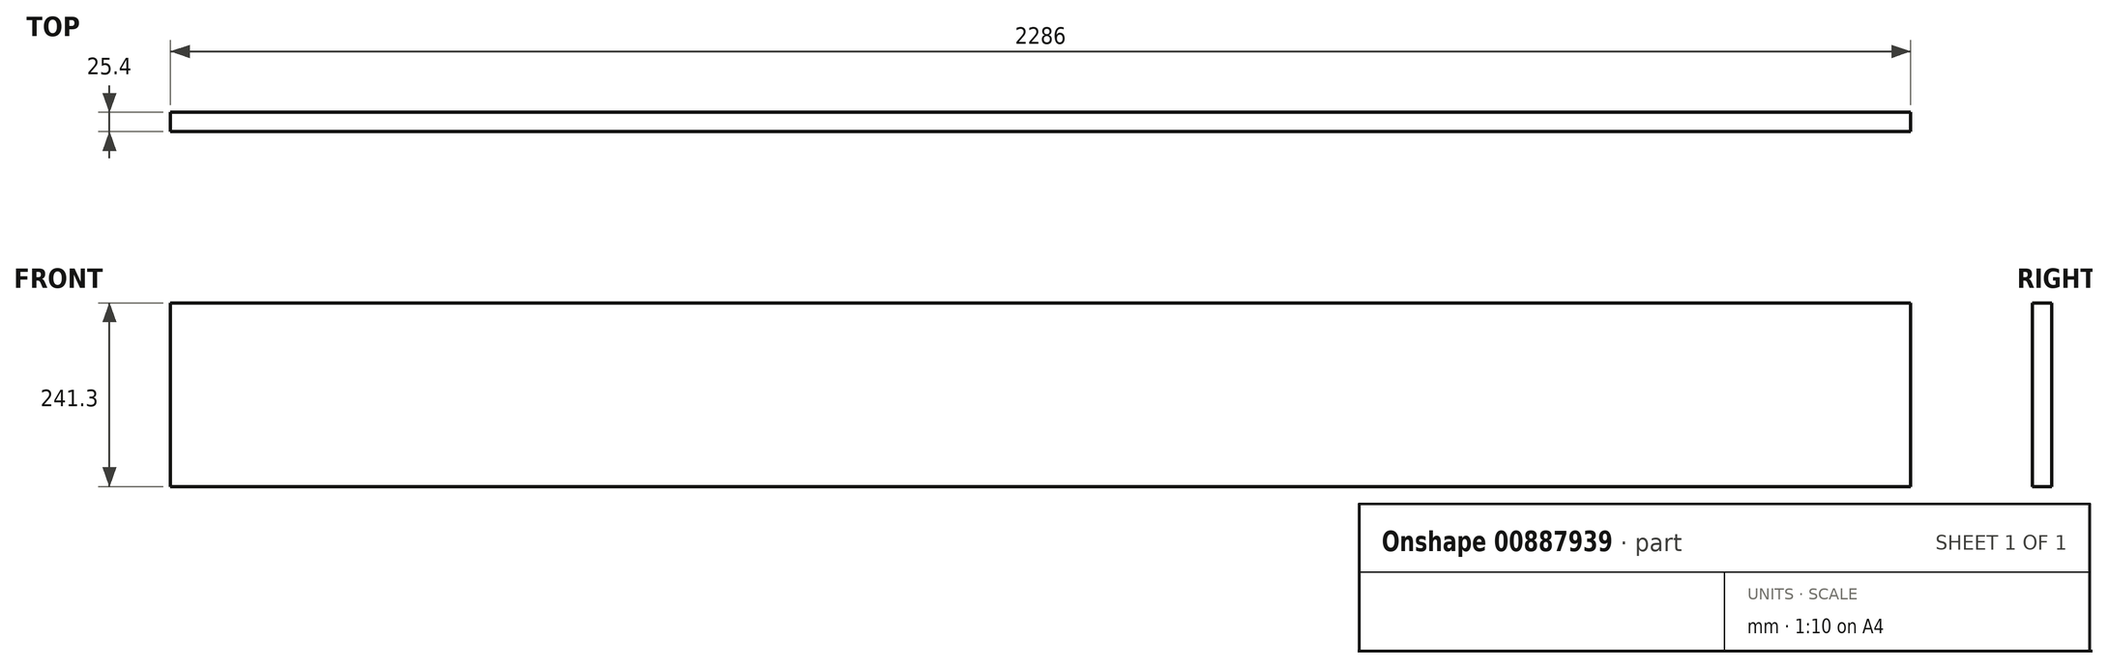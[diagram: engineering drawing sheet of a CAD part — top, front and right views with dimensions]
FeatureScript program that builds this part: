
annotation { "Feature Type Name" : "Feature", "Feature Type Description" : "" }
export const myFeature = defineFeature(function(context is Context, id is Id, definition is map)
    precondition{}
    {
        {
            var Q0;
            Q0=qCreatedBy(makeId("Front.planeOp"),FACE);
            var sketch = newSketch(context, id + "F0", { "sketchPlane" : qUnion([Q0])});
            skLineSegment(sketch, "E0.bottom", {"start": v(0, 0) * mm, "end": v(2286, 0) * mm});
            skLineSegment(sketch, "E0.top", {"start": v(0, 241.3) * mm, "end": v(2286, 241.3) * mm});
            skLineSegment(sketch, "E0.left", {"start": v(0, 0) * mm, "end": v(0, 241.3) * mm});
            skLineSegment(sketch, "E0.right", {"start": v(2286, 0) * mm, "end": v(2286, 241.3) * mm});
            skSolve(sketch);
        }
        {
            var Q0;
            Q0 = qSketchRegion(id + "F0", true);
            extrude(context, id + "F1", {"entities" : qUnion([Q0]), "depth" : 25.4 * mm, "offsetDistance" : 25.4 * mm});
        }
    });
